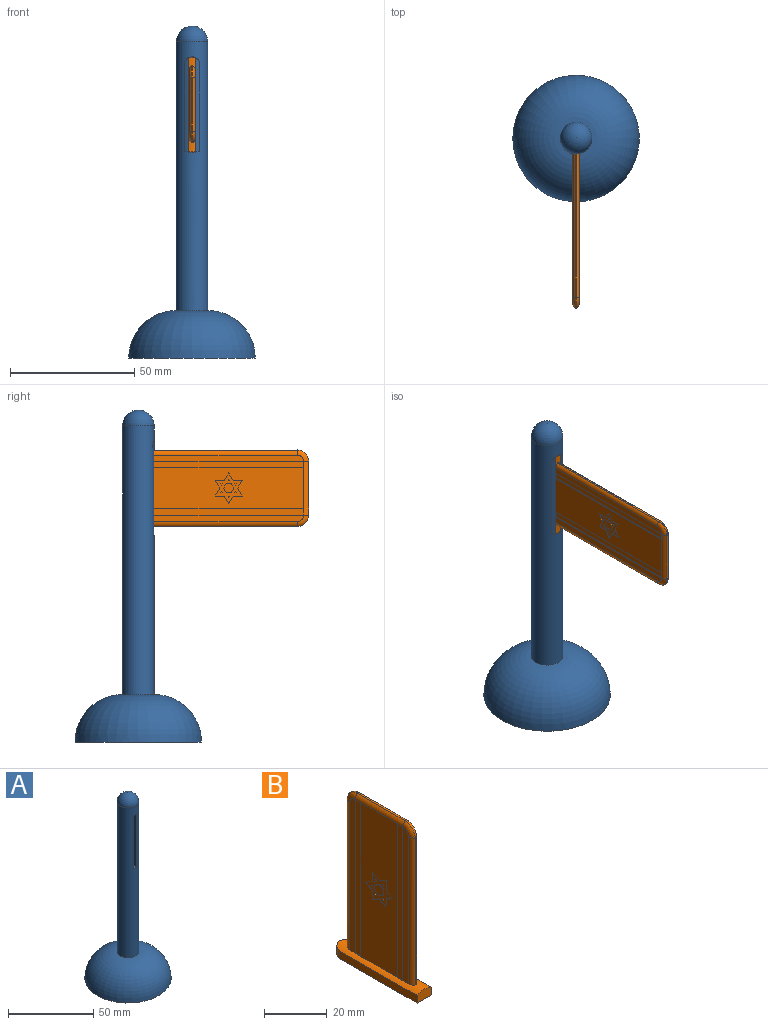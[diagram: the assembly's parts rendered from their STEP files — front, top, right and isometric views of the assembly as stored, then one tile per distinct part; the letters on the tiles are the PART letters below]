
ASSEMBLY  parts=2 mates=1
PART A: 9 faces, bbox 50.8x50.8x133.4 mm
  f0: cylinder r=6.35mm len=107.95mm, axis (0,0,-1), area 4209.6mm2, adj f2,f3,f4,f5,f6,f7
  f1: plane 50.8x50.8mm, normal (0,0,-1), area 2026.8mm2, adj f2
  f2: torus R=6.35mm, axis (0,0,-1), area 3474.1mm2, adj f0,f1
  f3: sphere r=6.35mm, area 253.4mm2, adj f0
  f4: plane 38.1x3.68mm, normal (1,0,0), area 140.3mm2, adj f0,f5,f7,f8
  f5: plane 3.81x2.54mm, normal (0,0,1), area 9.6mm2, adj f0,f4,f6,f8
  f6: plane 38.1x3.68mm, normal (-1,0,0), area 140.3mm2, adj f0,f5,f7,f8
  f7: plane 3.81x2.54mm, normal (0,0,-1), area 9.6mm2, adj f0,f4,f6,f8
  f8: plane 38.1x2.54mm, normal (0,-1,0), area 96.8mm2, adj f4,f5,f6,f7
PART B: 135 faces, bbox 6.4x38.1x66.8 mm
  f0: plane 60.24x2.54mm, normal (1,0,0), area 151.6mm2, adj f9,f17,f19,f130
  f1: plane 60.24x16.51mm, normal (1,0,0), area 927.8mm2, adj f9,f15,f80,f81,f82,f83,f84,f85
  f2: plane 60.24x16.51mm, normal (-1,0,0), area 927.8mm2, adj f9,f16,f36,f37,f38,f39,f40,f41
  f3: plane 60.24x2.54mm, normal (-1,0,0), area 151.6mm2, adj f9,f18,f20,f69
  f4: plane 60.24x2.54mm, normal (-1,0,0), area 151.6mm2, adj f9,f12,f14,f75
  f5: cylinder r=3.17mm len=6.35mm, axis (0,0,-1), area 33.5mm2, adj f6,f8,f9,f134
  f6: plane 34.93x2.92mm, normal (-1,0,0), area 102mm2, adj f5,f7,f9,f134
  f7: plane 6.35x3.77mm, normal (0,-1,0), area 22.2mm2, adj f6,f8,f9,f134
  f8: plane 34.93x2.92mm, normal (1,0,0), area 102mm2, adj f5,f7,f9,f134
  f9: cylinder r=6.35mm len=38.1mm, axis (0,-1,0), area 172.5mm2, adj f0,f1,f2,f3,f4,f5,f6,f7
  f10: plane 60.24x2.54mm, normal (1,0,0), area 151.6mm2, adj f9,f11,f13,f124
  f11: cylinder r=2.54mm len=57.7mm, axis (0,0,1), area 131.1mm2, adj f9,f10,f13,f21
  f12: cylinder r=2.54mm len=57.7mm, axis (0,0,-1), area 131.1mm2, adj f4,f9,f14,f21
  f13: torus R=2.54mm, axis (-1,0,0), area 12.9mm2, adj f10,f11,f15,f22
  f14: torus R=2.54mm, axis (-1,0,0), area 12.9mm2, adj f4,f12,f16,f22
  f15: cylinder r=2.54mm len=21.59mm, axis (0,-1,0), area 49.1mm2, adj f1,f13,f17,f23,f125,f129
  f16: cylinder r=2.54mm len=21.59mm, axis (0,1,0), area 49.1mm2, adj f2,f14,f18,f23,f70,f74
  f17: torus R=2.54mm, axis (-1,0,0), area 12.9mm2, adj f0,f15,f19,f24
  f18: torus R=2.54mm, axis (-1,0,0), area 12.9mm2, adj f3,f16,f20,f24
  f19: cylinder r=2.54mm len=57.7mm, axis (0,0,-1), area 131.1mm2, adj f0,f9,f17,f25
  f20: cylinder r=2.54mm len=57.7mm, axis (0,0,1), area 131.1mm2, adj f3,f9,f18,f25
  f21: cylinder r=0.51mm len=57.58mm, axis (0,0,-1), area 39.5mm2, adj f9,f11,f12,f22
  f22: torus R=4.13mm, axis (1,0,0), area 5mm2, adj f13,f14,f21,f23
  f23: cylinder r=0.51mm len=21.59mm, axis (0,1,0), area 14.8mm2, adj f15,f16,f22,f24
  f24: torus R=4.13mm, axis (1,0,0), area 5mm2, adj f17,f18,f23,f25
  f25: cylinder r=0.51mm len=57.58mm, axis (0,0,1), area 39.5mm2, adj f9,f19,f20,f24
  f26: plane 0.61x0.35mm, normal (0,-0.5,0.87), area 0.2mm2, adj f27,f61,f62,f79
  f27: plane 0.61x0.35mm, normal (0,-0.5,-0.87), area 0.2mm2, adj f26,f61,f62,f79
  f28: plane 0.47x0.27mm, normal (0,0.5,0.87), area 0.1mm2, adj f29,f54,f62,f68
  f29: plane 0.54x0.25mm, normal (0,-1,0), area 0.1mm2, adj f28,f54,f62,f68
  f30: plane 0.61x0.35mm, normal (0,-0.5,0.87), area 0.2mm2, adj f31,f55,f62,f67
  f31: plane 0.61x0.35mm, normal (0,-0.5,-0.87), area 0.2mm2, adj f30,f55,f62,f67
  f32: plane 0.7x0.25mm, normal (0,-1,0), area 0.2mm2, adj f33,f56,f62,f66
  f33: plane 0.61x0.35mm, normal (0,0.5,-0.87), area 0.2mm2, adj f32,f56,f62,f66
  f34: plane 0.47x0.27mm, normal (0,-0.5,-0.87), area 0.1mm2, adj f35,f57,f62,f65
  f35: plane 0.54x0.25mm, normal (0,1,0), area 0.1mm2, adj f34,f57,f62,f65
  f36: plane 3.15x1.82mm, normal (0,0.5,0.87), area 0.9mm2, adj f2,f37,f58,f62
  f37: plane 3.15x1.82mm, normal (0,-0.5,0.87), area 0.9mm2, adj f2,f36,f38,f62
  f38: plane 3.64x0.25mm, normal (0,1,0), area 0.9mm2, adj f2,f37,f39,f62
  f39: plane 3.01x1.74mm, normal (0,0.5,0.87), area 0.9mm2, adj f2,f38,f40,f62
  f40: plane 3.01x1.74mm, normal (0,0.5,-0.87), area 0.9mm2, adj f2,f39,f41,f62
  f41: plane 3.64x0.25mm, normal (0,1,0), area 0.9mm2, adj f2,f40,f42,f62
  f42: plane 3.15x1.82mm, normal (0,-0.5,-0.87), area 0.9mm2, adj f2,f41,f43,f62
  f43: plane 3.15x1.82mm, normal (0,0.5,-0.87), area 0.9mm2, adj f2,f42,f44,f62
  f44: plane 3.64x0.25mm, normal (0,-1,0), area 0.9mm2, adj f2,f43,f45,f62
  f45: plane 3.01x1.74mm, normal (0,-0.5,-0.87), area 0.9mm2, adj f2,f44,f46,f62
  f46: plane 3.01x1.74mm, normal (0,-0.5,0.87), area 0.9mm2, adj f2,f45,f58,f62
  f47: plane 0.61x0.35mm, normal (0,0.5,-0.87), area 0.2mm2, adj f48,f59,f62,f64
  f48: plane 0.61x0.35mm, normal (0,0.5,0.87), area 0.2mm2, adj f47,f59,f62,f64
  f49: plane 1.88x1.09mm, normal (0,-0.5,-0.87), area 0.6mm2, adj f50,f60,f62,f63
  f50: plane 1.88x1.09mm, normal (0,0.5,-0.87), area 0.6mm2, adj f49,f51,f62,f63
  f51: plane 2.01x0.25mm, normal (0,1,0), area 0.5mm2, adj f50,f52,f62,f63
  f52: plane 1.88x1.09mm, normal (0,0.5,0.87), area 0.6mm2, adj f51,f53,f62,f63
  f53: plane 1.88x1.09mm, normal (0,-0.5,0.87), area 0.6mm2, adj f52,f60,f62,f63
  f54: plane 0.47x0.27mm, normal (0,0.5,-0.87), area 0.1mm2, adj f28,f29,f62,f68
  f55: plane 0.7x0.25mm, normal (0,1,0), area 0.2mm2, adj f30,f31,f62,f67
  f56: plane 0.61x0.35mm, normal (0,0.5,0.87), area 0.2mm2, adj f32,f33,f62,f66
  f57: plane 0.47x0.27mm, normal (0,-0.5,0.87), area 0.1mm2, adj f34,f35,f62,f65
  f58: plane 3.64x0.25mm, normal (0,-1,0), area 0.9mm2, adj f2,f36,f46,f62
  f59: plane 0.7x0.25mm, normal (0,-1,0), area 0.2mm2, adj f47,f48,f62,f64
  f60: plane 2.01x0.25mm, normal (0,-1,0), area 0.5mm2, adj f49,f53,f62,f63
  f61: plane 0.7x0.25mm, normal (0,1,0), area 0.2mm2, adj f26,f27,f62,f79
  f62: plane 12.32x10.75mm, normal (-1,0,0), area 54mm2, adj f26,f27,f28,f29,f30,f31,f32,f33
  f63: plane 4.18x3.76mm, normal (-1,0,0), area 11.6mm2, adj f49,f50,f51,f52,f53,f60
  f64: plane 0.7x0.61mm, normal (-1,0,0), area 0.2mm2, adj f47,f48,f59
  f65: plane 0.54x0.47mm, normal (-1,0,0), area 0.1mm2, adj f34,f35,f57
  f66: plane 0.7x0.61mm, normal (-1,0,0), area 0.2mm2, adj f32,f33,f56
  f67: plane 0.7x0.61mm, normal (-1,0,0), area 0.2mm2, adj f30,f31,f55
  f68: plane 0.54x0.47mm, normal (-1,0,0), area 0.1mm2, adj f28,f29,f54
  f69: plane 60.24x0.25mm, normal (0,1,0), area 15.3mm2, adj f3,f70,f72,f73
  f70: plane 2.54x0.25mm, normal (0,0,-1), area 0.6mm2, adj f16,f69,f71,f73
  f71: plane 60.24x0.25mm, normal (0,-1,0), area 15.3mm2, adj f2,f70,f72,f73
  f72: plane 2.54x0.25mm, normal (0,0,1), area 0.6mm2, adj f9,f69,f71,f73
  f73: plane 60.24x2.54mm, normal (-1,0,0), area 153mm2, adj f69,f70,f71,f72
  f74: plane 2.54x0.25mm, normal (0,0,-1), area 0.6mm2, adj f16,f75,f77,f78
  f75: plane 60.24x0.25mm, normal (0,-1,0), area 15.3mm2, adj f4,f74,f76,f78
  f76: plane 2.54x0.25mm, normal (0,0,1), area 0.6mm2, adj f9,f75,f77,f78
  f77: plane 60.24x0.25mm, normal (0,1,0), area 15.3mm2, adj f2,f74,f76,f78
  f78: plane 60.24x2.54mm, normal (-1,0,0), area 153mm2, adj f74,f75,f76,f77
  f79: plane 0.7x0.61mm, normal (-1,0,0), area 0.2mm2, adj f26,f27,f61
  f80: plane 3.14x1.81mm, normal (0,0.5,0.87), area 0.9mm2, adj f1,f81,f115,f116
  f81: plane 3.56x0.25mm, normal (0,1,0), area 0.9mm2, adj f1,f80,f82,f116
  f82: plane 3.09x1.78mm, normal (0,-0.5,0.87), area 0.9mm2, adj f1,f81,f83,f116
  f83: plane 3.09x1.78mm, normal (0,0.5,0.87), area 0.9mm2, adj f1,f82,f84,f116
  f84: plane 3.56x0.25mm, normal (0,-1,0), area 0.9mm2, adj f1,f83,f85,f116
  f85: plane 3.14x1.81mm, normal (0,-0.5,0.87), area 0.9mm2, adj f1,f84,f86,f116
  f86: plane 3.14x1.81mm, normal (0,-0.5,-0.87), area 0.9mm2, adj f1,f85,f87,f116
  f87: plane 3.56x0.25mm, normal (0,-1,0), area 0.9mm2, adj f1,f86,f88,f116
  f88: plane 3.09x1.78mm, normal (0,0.5,-0.87), area 0.9mm2, adj f1,f87,f89,f116
  f89: plane 3.09x1.78mm, normal (0,-0.5,-0.87), area 0.9mm2, adj f1,f88,f90,f116
  f90: plane 3.56x0.25mm, normal (0,1,0), area 0.9mm2, adj f1,f89,f115,f116
  f91: plane 0.69x0.25mm, normal (0,1,0), area 0.2mm2, adj f92,f108,f116,f123
  f92: plane 0.6x0.34mm, normal (0,-0.5,-0.87), area 0.2mm2, adj f91,f108,f116,f123
  f93: plane 0.55x0.32mm, normal (0,-0.5,-0.87), area 0.2mm2, adj f94,f109,f116,f122
  f94: plane 0.55x0.32mm, normal (0,-0.5,0.87), area 0.2mm2, adj f93,f109,f116,f122
  f95: plane 0.55x0.32mm, normal (0,0.5,0.87), area 0.2mm2, adj f96,f110,f116,f121
  f96: plane 0.55x0.32mm, normal (0,0.5,-0.87), area 0.2mm2, adj f95,f110,f116,f121
  f97: plane 0.55x0.32mm, normal (0,-0.5,-0.87), area 0.2mm2, adj f98,f111,f116,f120
  f98: plane 0.55x0.32mm, normal (0,-0.5,0.87), area 0.2mm2, adj f97,f111,f116,f120
  f99: plane 0.69x0.25mm, normal (0,-1,0), area 0.2mm2, adj f100,f112,f116,f119
  f100: plane 0.6x0.34mm, normal (0,0.5,0.87), area 0.2mm2, adj f99,f112,f116,f119
  f101: plane 0.55x0.32mm, normal (0,0.5,0.87), area 0.2mm2, adj f102,f113,f116,f118
  f102: plane 0.55x0.32mm, normal (0,0.5,-0.87), area 0.2mm2, adj f101,f113,f116,f118
  f103: plane 1.82x1.05mm, normal (0,-0.5,0.87), area 0.5mm2, adj f104,f114,f116,f117
  f104: plane 1.82x1.05mm, normal (0,0.5,0.87), area 0.5mm2, adj f103,f105,f116,f117
  f105: plane 2.16x0.25mm, normal (0,1,0), area 0.5mm2, adj f104,f106,f116,f117
  f106: plane 1.82x1.05mm, normal (0,0.5,-0.87), area 0.5mm2, adj f105,f107,f116,f117
  f107: plane 1.82x1.05mm, normal (0,-0.5,-0.87), area 0.5mm2, adj f106,f114,f116,f117
  f108: plane 0.6x0.34mm, normal (0,-0.5,0.87), area 0.2mm2, adj f91,f92,f116,f123
  f109: plane 0.63x0.25mm, normal (0,1,0), area 0.2mm2, adj f93,f94,f116,f122
  f110: plane 0.63x0.25mm, normal (0,-1,0), area 0.2mm2, adj f95,f96,f116,f121
  f111: plane 0.63x0.25mm, normal (0,1,0), area 0.2mm2, adj f97,f98,f116,f120
  f112: plane 0.6x0.34mm, normal (0,0.5,-0.87), area 0.2mm2, adj f99,f100,f116,f119
  f113: plane 0.63x0.25mm, normal (0,-1,0), area 0.2mm2, adj f101,f102,f116,f118
  f114: plane 2.16x0.25mm, normal (0,-1,0), area 0.5mm2, adj f103,f107,f116,f117
  f115: plane 3.14x1.81mm, normal (0,0.5,-0.87), area 0.9mm2, adj f1,f80,f90,f116
  f116: plane 12.45x10.75mm, normal (1,0,0), area 54mm2, adj f80,f81,f82,f83,f84,f85,f86,f87
  f117: plane 4.25x3.63mm, normal (1,0,0), area 11.6mm2, adj f103,f104,f105,f106,f107,f114
  f118: plane 0.63x0.55mm, normal (1,0,0), area 0.2mm2, adj f101,f102,f113
  f119: plane 0.69x0.6mm, normal (1,0,0), area 0.2mm2, adj f99,f100,f112
  f120: plane 0.63x0.55mm, normal (1,0,0), area 0.2mm2, adj f97,f98,f111
  f121: plane 0.63x0.55mm, normal (1,0,0), area 0.2mm2, adj f95,f96,f110
  f122: plane 0.63x0.55mm, normal (1,0,0), area 0.2mm2, adj f93,f94,f109
  f123: plane 0.69x0.6mm, normal (1,0,0), area 0.2mm2, adj f91,f92,f108
  f124: plane 60.24x0.25mm, normal (0,-1,0), area 15.3mm2, adj f10,f125,f127,f128
  f125: plane 2.54x0.25mm, normal (0,0,-1), area 0.6mm2, adj f15,f124,f126,f128
  f126: plane 60.24x0.25mm, normal (0,1,0), area 15.3mm2, adj f1,f125,f127,f128
  f127: plane 2.54x0.25mm, normal (0,0,1), area 0.6mm2, adj f9,f124,f126,f128
  f128: plane 60.24x2.54mm, normal (1,0,0), area 153mm2, adj f124,f125,f126,f127
  f129: plane 2.54x0.25mm, normal (0,0,-1), area 0.6mm2, adj f15,f130,f132,f133
  f130: plane 60.24x0.25mm, normal (0,1,0), area 15.3mm2, adj f0,f129,f131,f133
  f131: plane 2.54x0.25mm, normal (0,0,1), area 0.6mm2, adj f9,f130,f132,f133
  f132: plane 60.24x0.25mm, normal (0,-1,0), area 15.3mm2, adj f1,f129,f131,f133
  f133: plane 60.24x2.54mm, normal (1,0,0), area 153mm2, adj f129,f130,f131,f132
  f134: plane 38.1x6.35mm, normal (0,0,-1), area 237.6mm2, adj f5,f6,f7,f8
PLACE A t=(0,-25.02,-0.42)mm
PLACE B rot(axis=(1,0,0),90deg) t=(0,-27.94,82.46)mm
MATE fastened B.f134 <-> A.f8  axis (0,1,0) through (0,-27.56,101.18)mm
